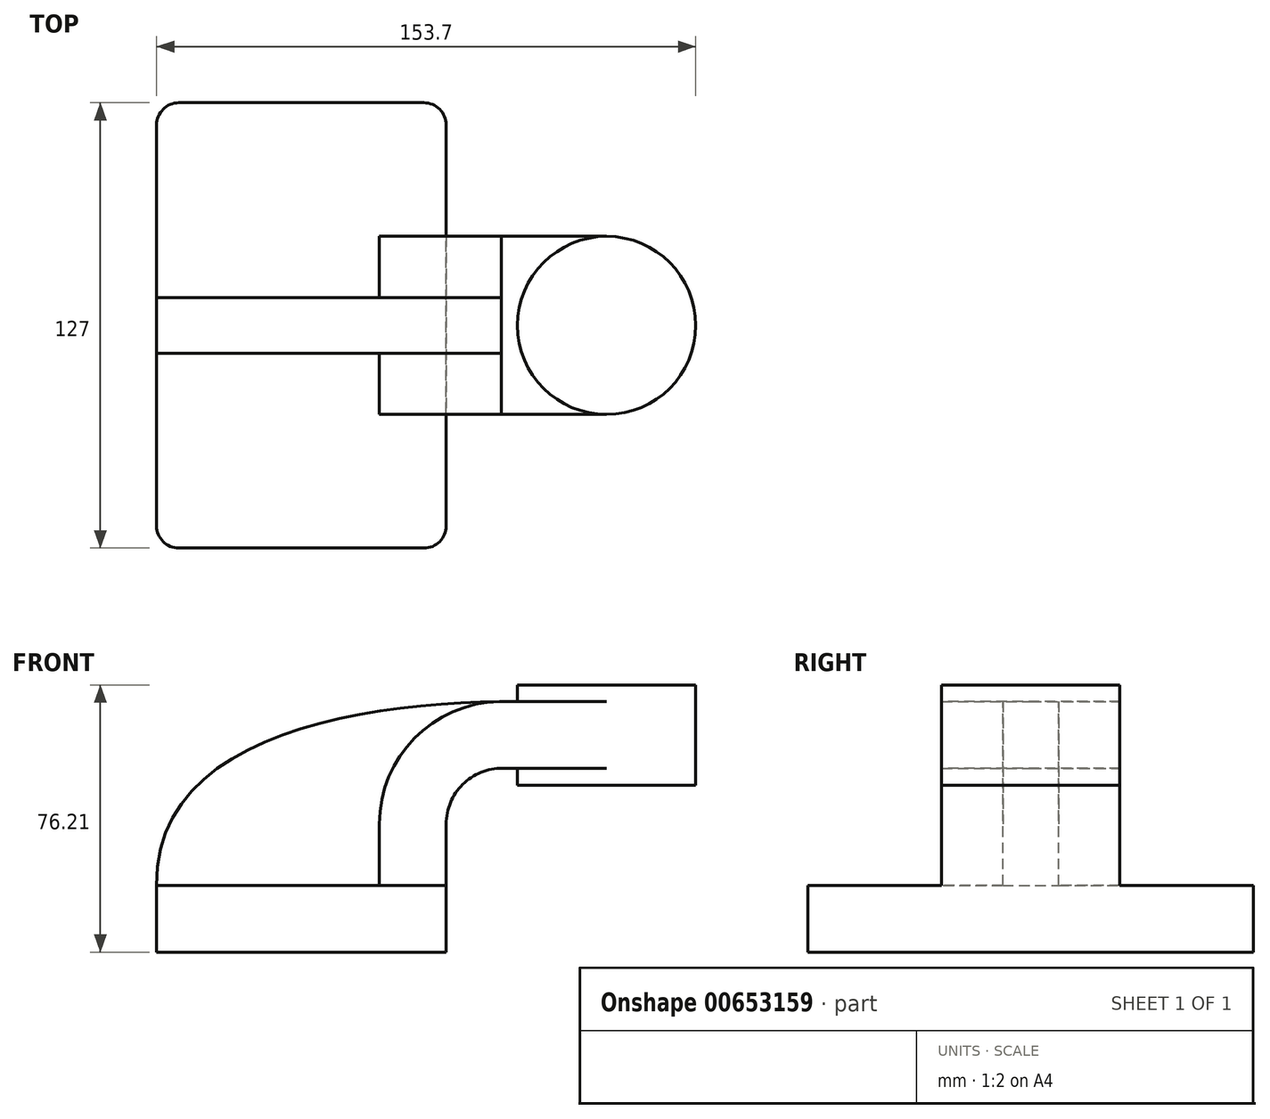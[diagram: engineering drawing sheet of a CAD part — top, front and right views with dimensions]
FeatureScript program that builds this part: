
annotation { "Feature Type Name" : "Feature", "Feature Type Description" : "" }
export const myFeature = defineFeature(function(context is Context, id is Id, definition is map)
    precondition{}
    {
        {
            var Q0;
            Q0=qCreatedBy(makeId("Front.planeOp"),FACE);
            var sketch = newSketch(context, id + "F0", { "sketchPlane" : qUnion([Q0])});
            skLineSegment(sketch, "E0.bottom", {"start": v(41.27, -9.52) * mm, "end": v(-41.27, -9.52) * mm});
            skLineSegment(sketch, "E0.top", {"start": v(41.27, 9.53) * mm, "end": v(-41.27, 9.53) * mm});
            skLineSegment(sketch, "E0.left", {"start": v(41.28, -9.52) * mm, "end": v(41.28, 9.53) * mm});
            skLineSegment(sketch, "E0.right", {"start": v(-41.27, -9.52) * mm, "end": v(-41.27, 9.53) * mm});
            skPoint(sketch, "E0.middle", {"position": v(0, 0) * mm});
            skLineSegment(sketch, "E1", {"start": v(41.27, 9.53) * mm, "end": v(41.27, 27) * mm});
            skArc(sketch, "E2", {"start": v(41.28, 27) * mm, "mid": v(45.97, 38.28) * mm, "end": v(57.3, 42.88) * mm});
            skLineSegment(sketch, "E3.bottom", {"start": v(112.42, 38.1) * mm, "end": v(61.62, 38.1) * mm});
            skLineSegment(sketch, "E3.top", {"start": v(112.42, 66.68) * mm, "end": v(61.62, 66.68) * mm});
            skLineSegment(sketch, "E3.left", {"start": v(112.42, 38.1) * mm, "end": v(112.42, 66.68) * mm});
            skLineSegment(sketch, "E3.right", {"start": v(61.62, 38.1) * mm, "end": v(61.62, 66.68) * mm});
            skPoint(sketch, "E3.middle", {"position": v(87.02, 52.39) * mm});
            skLineSegment(sketch, "E4", {"start": v(57.3, 42.88) * mm, "end": v(87.02, 42.88) * mm});
            skLineSegment(sketch, "E5.0", {"start": v(56.94, 61.93) * mm, "end": v(87.02, 61.93) * mm});
            skArc(sketch, "E5.1", {"start": v(22.23, 27) * mm, "mid": v(32.38, 51.62) * mm, "end": v(56.94, 61.93) * mm});
            skLineSegment(sketch, "E5.2", {"start": v(22.23, 9.53) * mm, "end": v(22.23, 27) * mm});
            skLineSegment(sketch, "E6", {"start": v(87.02, 66.68) * mm, "end": v(87.02, 38.1) * mm});
            skFitSpline(sketch, "E7", {"points": [v(-41.28, 9.53) * mm, v(56.94, 61.93) * mm], "startDerivative": vector(-1.81, 127.57) * mm, "endDerivative": vector(123.08, 1.39) * mm});
            skSolve(sketch);
        }
        {
            var Q0;
            Q0=makeQuery(id+"F0.imprint","IMPRINT",FACE,{"disambiguationData":[TD([[makeQuery(id+"F0.imprint","IMPRINT",EDGE,{"derivedFrom":sQuery(id+"F0.wireOp",EDGE,"E0.bottom")}),-1.0]])]});
            extrude(context, id + "F1", {"entities" : qUnion([Q0]), "endBound" : BoundingType.SYMMETRIC, "depth" : 127 * mm, "offsetDistance" : 25.4 * mm});
        }
        {
            var Q0;
            {var subQ5=sQuery(id+"F0.wireOp",EDGE,"E1");Q0=makeQuery(id+"F0.imprint","IMPRINT",FACE,{"disambiguationData":[TD([[makeQuery(id+"F0.imprint","IMPRINT",EDGE,{"derivedFrom":subQ5}),1.0]])]});}
            var Q1;
            {var subQ0=sQuery(id+"F0.wireOp",EDGE,"E4");var subQ1=sQuery(id+"F0.wireOp",EDGE,"E3.right");var subQ2=makeQuery(id+"F0.imprint","INTERSECT",VERTEX,{"derivedFrom":[subQ1,subQ0]});Q1=makeQuery(id+"F0.imprint","IMPRINT",FACE,{"disambiguationData":[TD([[makeQuery(id+"F0.imprint","IMPRINT",EDGE,{"disambiguationData":[TD([[subQ2,-1.0]])],"derivedFrom":subQ1}),-1.0]])]});}
            extrude(context, id + "F2", {"entities" : qUnion([Q0, Q1]), "operationType" : NewBodyOperationType.ADD, "endBound" : BoundingType.SYMMETRIC, "oppositeDirection" : true, "depth" : 50.8 * mm, "offsetDistance" : 25.4 * mm});
        }
        {
            var Q0;
            {var subQ3=sQuery(id+"F0.wireOp",EDGE,"E5.2");Q0=makeQuery(id+"F0.imprint","IMPRINT",FACE,{"disambiguationData":[TD([[makeQuery(id+"F0.imprint","IMPRINT",EDGE,{"derivedFrom":subQ3}),1.0]])]});}
            extrude(context, id + "F3", {"entities" : qUnion([Q0]), "operationType" : NewBodyOperationType.ADD, "endBound" : BoundingType.SYMMETRIC, "depth" : 15.88 * mm, "offsetDistance" : 25.4 * mm});
        }
        {
            var Q0;
            {var subQ0=sQuery(id+"F0.wireOp",EDGE,"E3.left");Q0=makeQuery(id+"F0.imprint","IMPRINT",FACE,{"disambiguationData":[TD([[makeQuery(id+"F0.imprint","IMPRINT",EDGE,{"derivedFrom":subQ0}),1.0]])]});}
            var Q1;
            Q1=sQuery(id+"F0.wireOp",EDGE,"E6");
            revolve(context, id + "F4", {"operationType" : NewBodyOperationType.ADD, "entities" : qUnion([Q0]), "axis" : qUnion([Q1]), "revolveType" : RevolveType.FULL, "oppositeDirection" : true});
        }
        {
            var Q0;
            Q0=makeQuery(id+"F1.opExtrude","CAP_EDGE",EDGE,{"disambiguationData":[OSD([sQuery(id+"F0.wireOp",EDGE,"E0.left")])],"isStart":true});
            var Q1;
            Q1=makeQuery(id+"F1.opExtrude","CAP_EDGE",EDGE,{"disambiguationData":[OSD([sQuery(id+"F0.wireOp",EDGE,"E0.right")])],"isStart":true});
            var Q2;
            Q2=makeQuery(id+"F1.opExtrude","CAP_EDGE",EDGE,{"disambiguationData":[OSD([sQuery(id+"F0.wireOp",EDGE,"E0.right")])],"isStart":false});
            var Q3;
            Q3=makeQuery(id+"F1.opExtrude","CAP_EDGE",EDGE,{"disambiguationData":[OSD([sQuery(id+"F0.wireOp",EDGE,"E0.left")])],"isStart":false});
            fillet(context, id + "F5", {"entities" : qUnion([Q0, Q1, Q2, Q3]), "radius" : 6.35 * mm, "tangentPropagation" : true, "allowEdgeOverflow" : false});
        }
    });
